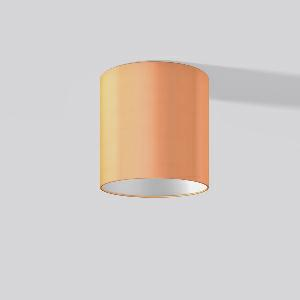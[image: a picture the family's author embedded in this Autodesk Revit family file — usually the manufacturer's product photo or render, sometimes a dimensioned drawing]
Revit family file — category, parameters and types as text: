
# Revit family: toledo_flatliner_901634_002_1_76_f2e0
name_source: partatom
category: Lighting Fixtures
units: mm (PartAtom-declared; Revit-internal decimal feet)

## family parameters
Cut with Voids When Loaded = No
Host = Face
Light Source = No
Part Type = Normal
Room Calculation Point = No
Round Connector Dimension = Use Diameter
Shared = No

## types (1)
- 982302.002 (1 x LED Modul 840, 1950 lm, 4000)
    Apparent Load = 22 VA
    CIE Flux Codes = 50 82 97 99 100
    Color Rendering = 80
    Color Temperature = 4000
    Default Elevation = 1800 mm
    Description = Series: TOLEDO FLATLINER
Decorative ceiling luminaire for interior decoration. Base luminaire prepared for the installation of fabric lampshade. Cylinder housing sheet steel, powder-coated. Housing: die cast aluminium and sheet steel, powder-coated. Bezel ring: die-cast aluminium, powder-coated. Lightguide and diffuser made of non-yellowing plastic (PMMA) opal matt. Modular design: With the basic luminaire, a square or cylindrical fabric lampshade must always be ordered separately. Fabric lampshades can be fitted to the basic luminaire without tools. Order satin finish diffuser as separate accessory. 
Colour: white
Diameter: 330 mm
Height: 70 mm
Lamp: LED
Socket: without socket
Colour temperature: 4000K
Colour rendering index (CRI): 80
System power: 22 W
Rated luminous flux: 1950 lm
Luminous efficiency: 89 lm/W
Control gear: Converter, dimmable, DALI
Protection class: II
Type of protection: IP 40
    Height = 70 mm
    Lamp = 1 x LED Modul 840
    Lamp Light Flux = 1950 lm
    Lamp count = 1
    Length = 330 mm
    Lifetime = 50000 h
    Luminous efficacy = 89 lm/W
    Manufacturer = RZB
    ModVariant = No
    Model = 901634.002.1.76
    Mounting Place = Ceiling
    Mounting Type = Surface mounted
    Number of Poles = 1
    OnlyDefault = Yes
    Power Factor = 1
    Product Name = TOLEDO FLATLINER
    Product group = Surface mounted ceiling Fabric lampshade luminaires
    ProductGroupID = 313
    Protection Class = Protection class II
    Protection Degree = IP 40
    RLX_Detail_Level = 1
    RLX_Emergency_Light_Flux = 0 lm
    RLX_Emergency_Type = 0
    RLX_Emergency_Type_DB = No
    RlxData = <blob elided: 62829 chars, md5=642cb9e2>
    Socket = socket
    Standby Power = 0 W
    System Light Flux = 1950 lm
    System Power = 22 W
    Type Image = toledo_flatliner_anbau_rund_orange_odeckel.jpg
    URL = http://relux.com
    VarID = 982302_002_891e
    Voltage = 230 V
    Voltage Range = 220-240 V
    Weight = 0.00 kg
    Width = 0 mm  [stored 0 ft]

note: [stored X ft] marks values corroborated as IEEE doubles in the binary element streams (Revit-internal decimal feet)

## geometry (parser evidence)
native form markers: Blend x4, Sweep x11
no freeform markers — native parametric forms only
